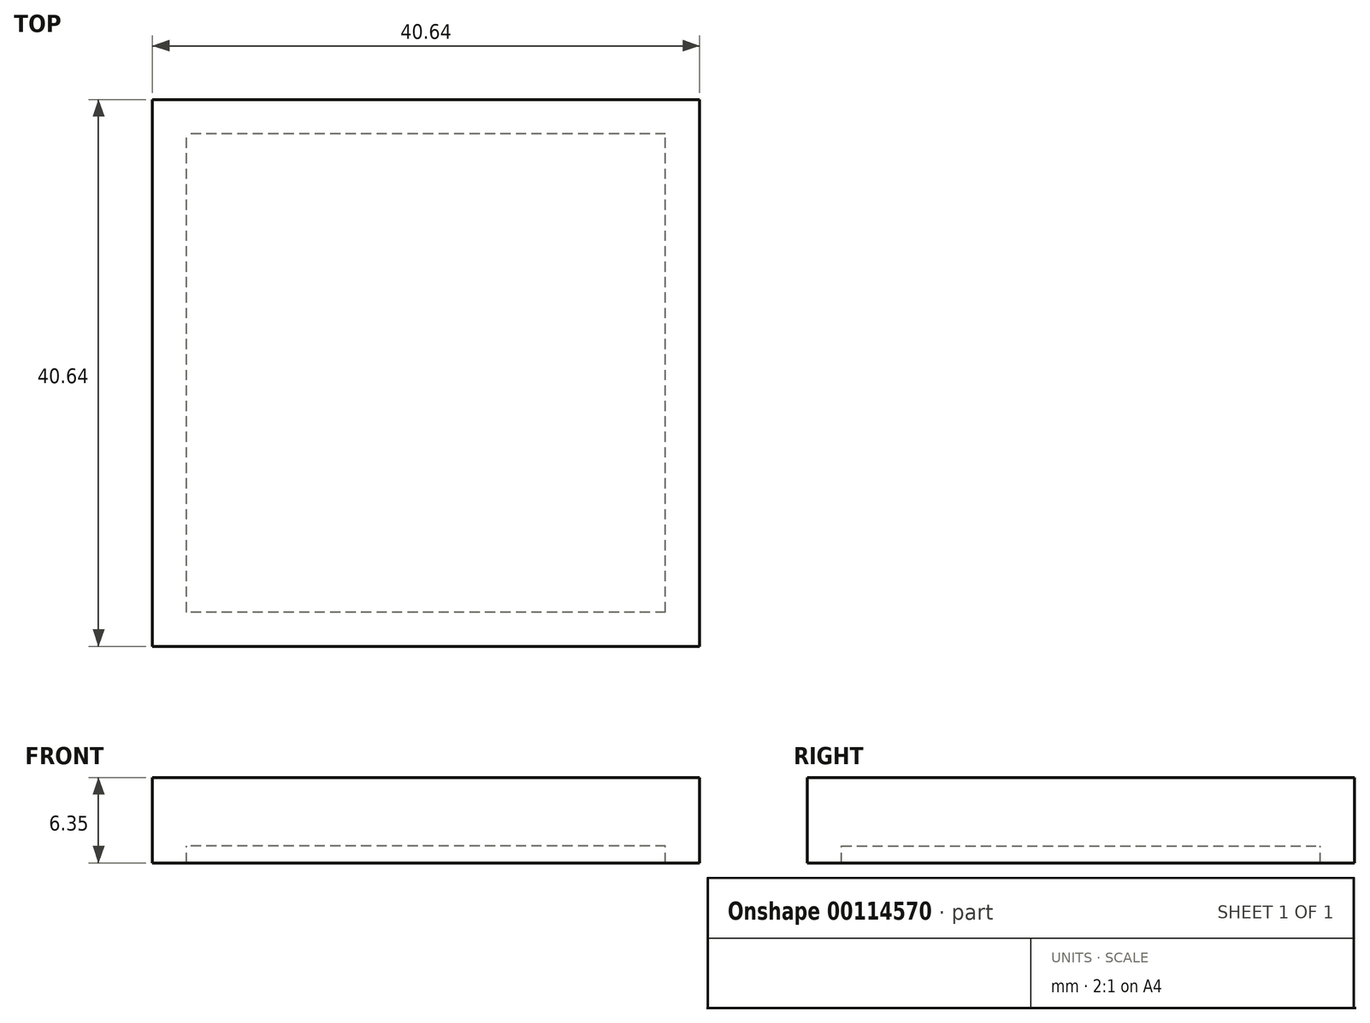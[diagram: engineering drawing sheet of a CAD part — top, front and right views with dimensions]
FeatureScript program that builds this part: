
annotation { "Feature Type Name" : "Feature", "Feature Type Description" : "" }
export const myFeature = defineFeature(function(context is Context, id is Id, definition is map)
    precondition{}
    {
        {
            var Q0;
            Q0=qCreatedBy(makeId("Top.planeOp"),FACE);
            var sketch = newSketch(context, id + "F0", { "sketchPlane" : qUnion([Q0])});
            skLineSegment(sketch, "E0.bottom", {"start": v(20.32, -20.32) * mm, "end": v(-20.32, -20.32) * mm});
            skLineSegment(sketch, "E0.top", {"start": v(20.32, 20.32) * mm, "end": v(-20.32, 20.32) * mm});
            skLineSegment(sketch, "E0.left", {"start": v(20.32, -20.32) * mm, "end": v(20.32, 20.32) * mm});
            skLineSegment(sketch, "E0.right", {"start": v(-20.32, -20.32) * mm, "end": v(-20.32, 20.32) * mm});
            skPoint(sketch, "E0.middle", {"position": v(0, 0) * mm});
            skLineSegment(sketch, "E1.bottom", {"start": v(17.78, -17.78) * mm, "end": v(-17.78, -17.78) * mm});
            skLineSegment(sketch, "E1.top", {"start": v(17.78, 17.78) * mm, "end": v(-17.78, 17.78) * mm});
            skLineSegment(sketch, "E1.left", {"start": v(17.78, -17.78) * mm, "end": v(17.78, 17.78) * mm});
            skLineSegment(sketch, "E1.right", {"start": v(-17.78, -17.78) * mm, "end": v(-17.78, 17.78) * mm});
            skSolve(sketch);
        }
        {
            var Q0;
            Q0 = qSketchRegion(id + "F0", true);
            extrude(context, id + "F1", {"entities" : qUnion([Q0]), "oppositeDirection" : true, "depth" : 1.27 * mm});
        }
        {
            var Q0;
            Q0=qCreatedBy(makeId("Top.planeOp"),FACE);
            var sketch = newSketch(context, id + "F2", { "sketchPlane" : qUnion([Q0])});
            skLineSegment(sketch, "E2.bottom", {"start": v(20.32, 20.32) * mm, "end": v(-20.32, 20.32) * mm});
            skLineSegment(sketch, "E2.top", {"start": v(20.32, -20.32) * mm, "end": v(-20.32, -20.32) * mm});
            skLineSegment(sketch, "E2.left", {"start": v(20.32, 20.32) * mm, "end": v(20.32, -20.32) * mm});
            skLineSegment(sketch, "E2.right", {"start": v(-20.32, 20.32) * mm, "end": v(-20.32, -20.32) * mm});
            skPoint(sketch, "E2.middle", {"position": v(0, 0) * mm});
            skSolve(sketch);
        }
        {
            var Q0;
            Q0 = qSketchRegion(id + "F2", true);
            extrude(context, id + "F3", {"entities" : qUnion([Q0]), "operationType" : NewBodyOperationType.ADD, "depth" : 5.08 * mm});
        }
    });
